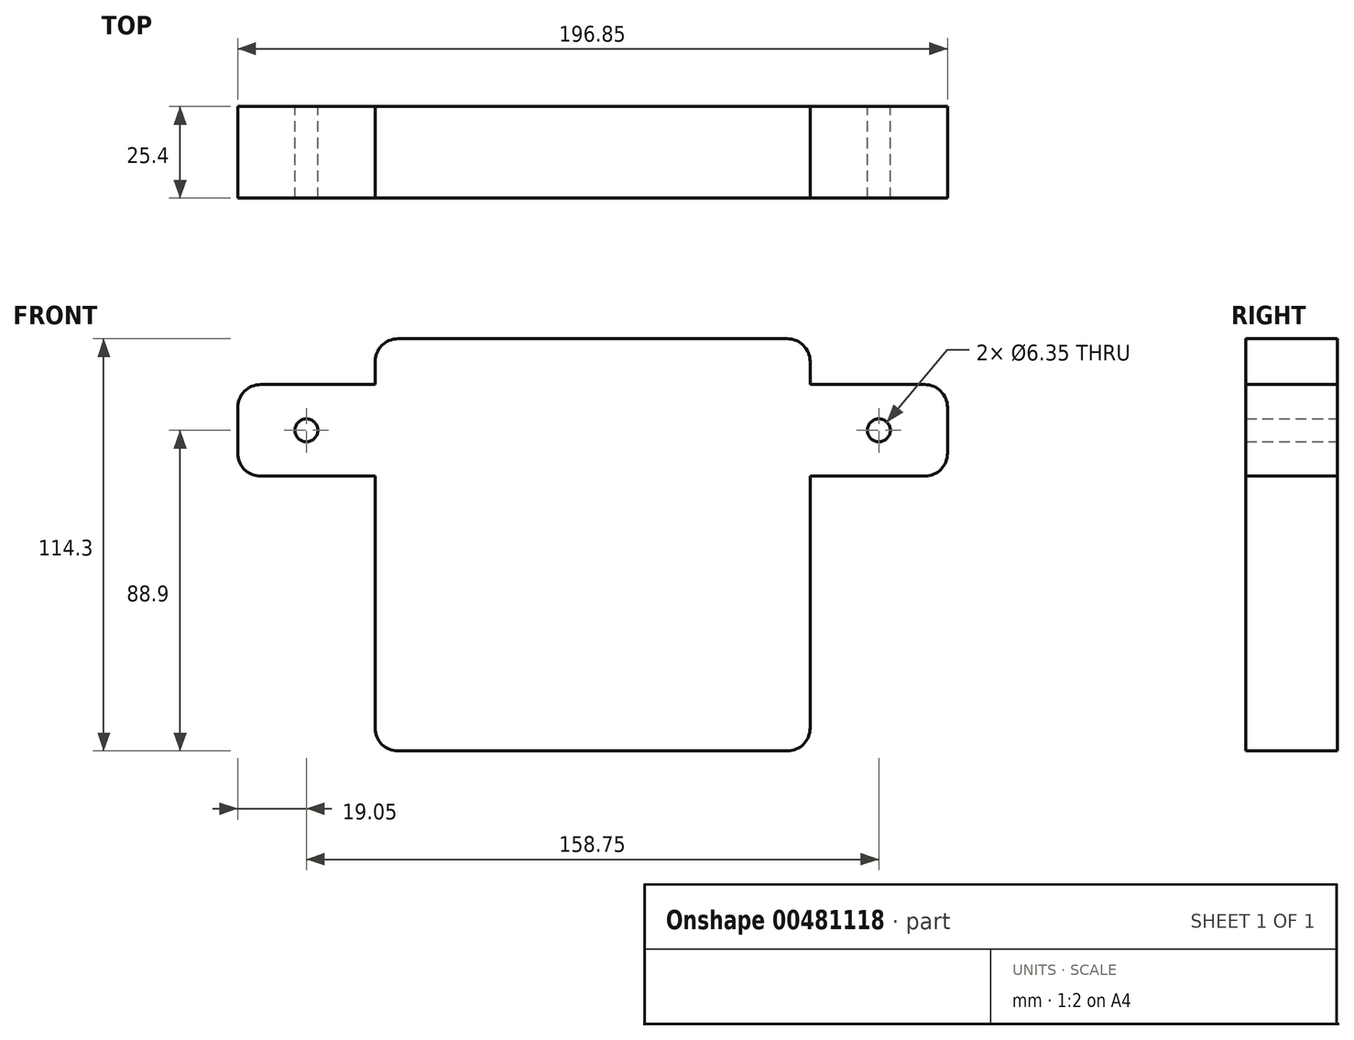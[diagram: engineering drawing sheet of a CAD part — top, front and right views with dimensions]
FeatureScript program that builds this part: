
annotation { "Feature Type Name" : "Feature", "Feature Type Description" : "" }
export const myFeature = defineFeature(function(context is Context, id is Id, definition is map)
    precondition{}
    {
        {
            var Q0;
            Q0=qCreatedBy(makeId("Front.planeOp"),FACE);
            var sketch = newSketch(context, id + "F0", { "sketchPlane" : qUnion([Q0])});
            skLineSegment(sketch, "E0.bottom", {"start": v(0, 0) * mm, "end": v(120.65, 0) * mm});
            skLineSegment(sketch, "E0.top", {"start": v(6.35, -76.2) * mm, "end": v(114.3, -76.2) * mm});
            skLineSegment(sketch, "E0.left", {"start": v(0, 0) * mm, "end": v(0, -69.85) * mm});
            skLineSegment(sketch, "E0.right", {"start": v(120.65, 0) * mm, "end": v(120.65, -69.85) * mm});
            skLineSegment(sketch, "E1.bottom", {"start": v(0, 0) * mm, "end": v(-31.75, 0) * mm});
            skLineSegment(sketch, "E1.top", {"start": v(0, 25.4) * mm, "end": v(-31.75, 25.4) * mm});
            skLineSegment(sketch, "E1.left", {"start": v(0, 0) * mm, "end": v(0, 25.4) * mm});
            skLineSegment(sketch, "E1.right", {"start": v(-38.1, 6.35) * mm, "end": v(-38.1, 19.05) * mm});
            skLineSegment(sketch, "E2.bottom", {"start": v(0, 25.4) * mm, "end": v(120.65, 25.4) * mm});
            skLineSegment(sketch, "E2.top", {"start": v(6.35, 38.1) * mm, "end": v(114.3, 38.1) * mm});
            skLineSegment(sketch, "E2.left", {"start": v(0, 25.4) * mm, "end": v(0, 31.75) * mm});
            skLineSegment(sketch, "E2.right", {"start": v(120.65, 25.4) * mm, "end": v(120.65, 31.75) * mm});
            skLineSegment(sketch, "E3.bottom", {"start": v(120.65, 25.4) * mm, "end": v(0, 25.4) * mm});
            skLineSegment(sketch, "E3.top", {"start": v(120.65, 0) * mm, "end": v(0, 0) * mm});
            skLineSegment(sketch, "E3.left", {"start": v(120.65, 25.4) * mm, "end": v(120.65, 0) * mm});
            skLineSegment(sketch, "E3.right", {"start": v(0, 25.4) * mm, "end": v(0, 0) * mm});
            skLineSegment(sketch, "E4.bottom", {"start": v(120.65, 25.4) * mm, "end": v(152.4, 25.4) * mm});
            skLineSegment(sketch, "E4.top", {"start": v(120.65, 0) * mm, "end": v(152.4, 0) * mm});
            skLineSegment(sketch, "E4.right", {"start": v(158.75, 19.05) * mm, "end": v(158.75, 6.35) * mm});
            skPoint(sketch, "E5.visualSharp", {"position": v(-38.1, 25.4) * mm});
            skArc(sketch, "E5.filletArc", {"start": v(-31.75, 25.4) * mm, "mid": v(-36.24, 23.54) * mm, "end": v(-38.1, 19.05) * mm});
            skPoint(sketch, "E6.visualSharp", {"position": v(-38.1, 0) * mm});
            skArc(sketch, "E6.filletArc", {"start": v(-38.1, 6.35) * mm, "mid": v(-36.24, 1.86) * mm, "end": v(-31.75, 0) * mm});
            skPoint(sketch, "E7.visualSharp", {"position": v(158.75, 25.4) * mm});
            skArc(sketch, "E7.filletArc", {"start": v(158.75, 19.05) * mm, "mid": v(156.9, 23.54) * mm, "end": v(152.4, 25.4) * mm});
            skPoint(sketch, "E8.visualSharp", {"position": v(158.75, 0) * mm});
            skArc(sketch, "E8.filletArc", {"start": v(152.4, 0) * mm, "mid": v(156.9, 1.86) * mm, "end": v(158.75, 6.35) * mm});
            skPoint(sketch, "E9.visualSharp", {"position": v(120.65, 38.1) * mm});
            skArc(sketch, "E9.filletArc", {"start": v(120.65, 31.75) * mm, "mid": v(118.8, 36.24) * mm, "end": v(114.3, 38.1) * mm});
            skPoint(sketch, "E10.visualSharp", {"position": v(0, 38.1) * mm});
            skArc(sketch, "E10.filletArc", {"start": v(6.35, 38.1) * mm, "mid": v(1.86, 36.24) * mm, "end": v(0, 31.75) * mm});
            skPoint(sketch, "E11.visualSharp", {"position": v(0, -76.2) * mm});
            skArc(sketch, "E11.filletArc", {"start": v(0, -69.85) * mm, "mid": v(1.86, -74.34) * mm, "end": v(6.35, -76.2) * mm});
            skPoint(sketch, "E12.visualSharp", {"position": v(120.65, -76.2) * mm});
            skArc(sketch, "E12.filletArc", {"start": v(114.3, -76.2) * mm, "mid": v(118.8, -74.34) * mm, "end": v(120.65, -69.85) * mm});
            skCircle(sketch, "E13", {"center": v(-19.05, 12.7) * mm, "radius": 3.18 * mm});
            skCircle(sketch, "E14", {"center": v(139.7, 12.7) * mm, "radius": 3.18 * mm});
            skPoint(sketch, "E15.centerSnap0", {"position": v(0, 12.7) * mm});
            skSolve(sketch);
        }
        {
            var Q0;
            Q0 = qSketchRegion(id + "F0", true);
            extrude(context, id + "F1", {"entities" : qUnion([Q0]), "depth" : 25.4 * mm});
        }
    });
